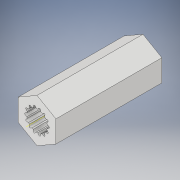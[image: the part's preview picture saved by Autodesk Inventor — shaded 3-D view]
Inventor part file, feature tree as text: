
AUTODESK INVENTOR PART (.ipt)
format: ipt  version: 2019.4 (Build 234330000, 330)  size: 769,536 bytes
history: native  units: in
note: dims shown in document units (in); Inventor stores cm internally (conversion verified against a paired STEP export)
features: extrude x3, sketch x3, projected_geometry x2, other x1
ambient origin geometry x8: Origin, YZ Plane, XZ Plane, XY Plane, X Axis, Y Axis, Z Axis, Center Point
bodies: Solid1 (feature_tree)
feature tree (9):
  extrude  "Extrusion1"  TaperAngle=0.0deg  [1 undecoded]
  extrude  "Extrusion2"  Depth=1.375in TaperAngle=0.0deg
  extrude  "Extrusion3"  [1 undecoded]
  sketch  "Sketch1"  dims[d1=0.49in d2=0.0in d3=0.0in]
  sketch  "Sketch2"  dims[d4=0.0in d5=0.0in d6=1.375in d7=0.0in]
  sketch  "Sketch3"  dims[d8=0.0035in]
  projected_geometry  "Projected Loop1"
  projected_geometry  "Projected Loop2"
  other  "Boss-Extrude2"
note: 2 required parameter values undecoded (feature->parameter linkage not recoverable at this tier; creation-order binding heuristic only, values carry confidence <= 0.55)
